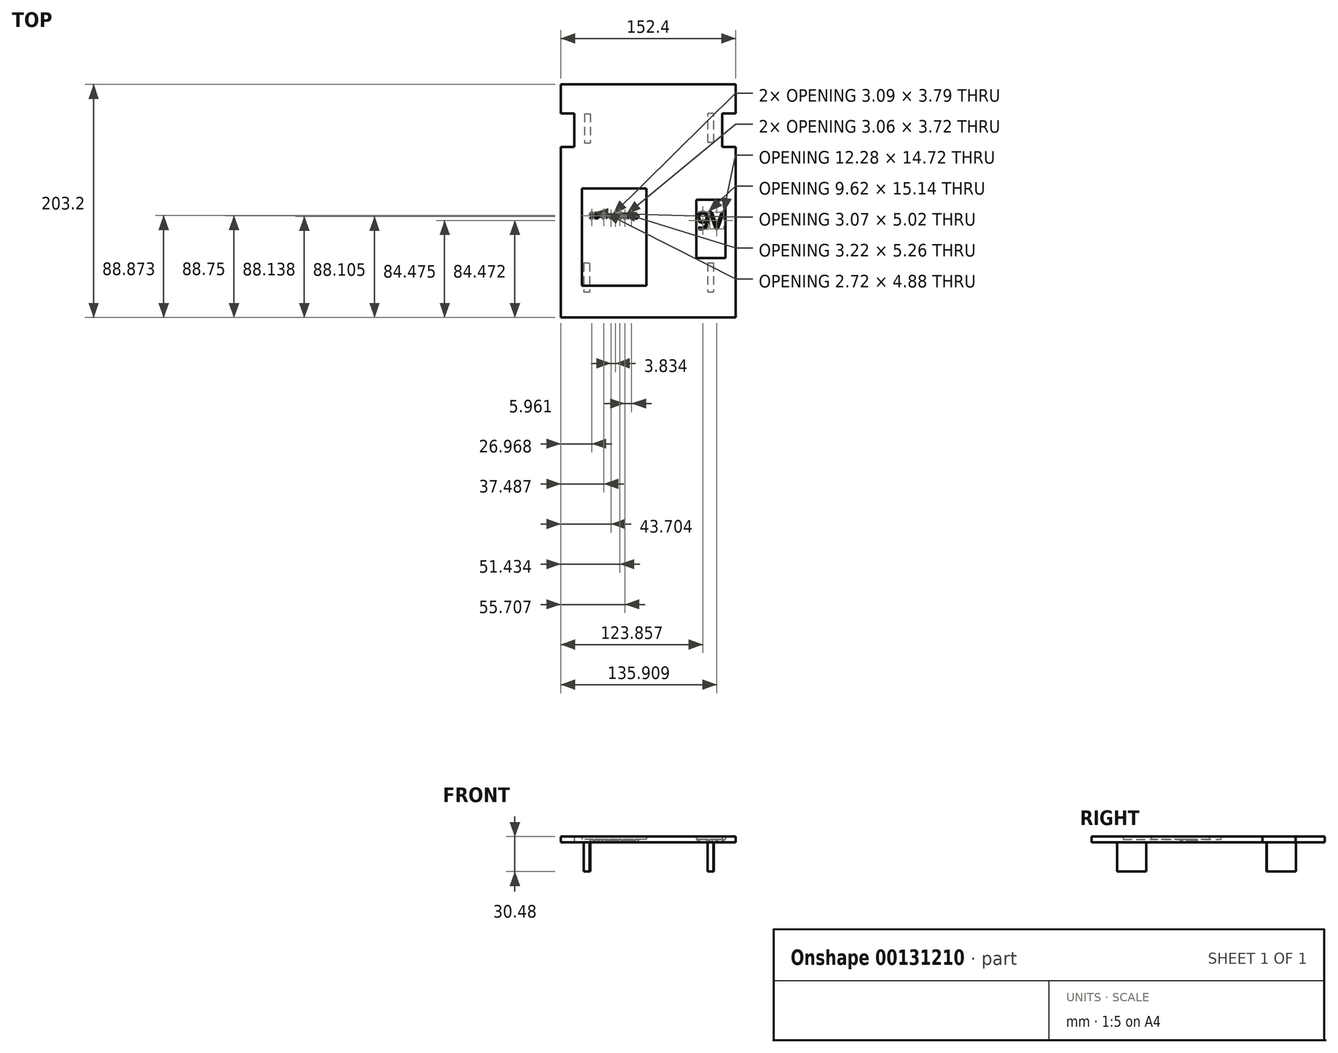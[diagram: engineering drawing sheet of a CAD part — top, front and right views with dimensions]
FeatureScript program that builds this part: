
annotation { "Feature Type Name" : "Feature", "Feature Type Description" : "" }
export const myFeature = defineFeature(function(context is Context, id is Id, definition is map)
    precondition{}
    {
        {
            var Q0;
            Q0=qCreatedBy(makeId("Top.planeOp"),FACE);
            var sketch = newSketch(context, id + "F0", { "sketchPlane" : qUnion([Q0])});
            skLineSegment(sketch, "E0.bottom", {"start": v(60.22, -89.13) * mm, "end": v(-92.18, -89.13) * mm});
            skLineSegment(sketch, "E0.top", {"start": v(60.22, 114.07) * mm, "end": v(-92.18, 114.07) * mm});
            skLineSegment(sketch, "E0.left", {"start": v(60.22, -89.13) * mm, "end": v(60.22, 114.07) * mm});
            skLineSegment(sketch, "E0.right", {"start": v(-92.18, -89.13) * mm, "end": v(-92.18, 114.07) * mm});
            skPoint(sketch, "E0.middle", {"position": v(-15.98, 12.47) * mm});
            skLineSegment(sketch, "E1.bottom", {"start": v(-92.18, 88.67) * mm, "end": v(-80.48, 88.67) * mm});
            skLineSegment(sketch, "E1.top", {"start": v(-92.18, 59.67) * mm, "end": v(-80.48, 59.67) * mm});
            skLineSegment(sketch, "E1.left", {"start": v(-92.18, 88.67) * mm, "end": v(-92.18, 59.67) * mm});
            skLineSegment(sketch, "E1.right", {"start": v(-80.48, 88.67) * mm, "end": v(-80.48, 59.67) * mm});
            skPoint(sketch, "E1.middle", {"position": v(-86.33, 74.17) * mm});
            skLineSegment(sketch, "E2.bottom", {"start": v(60.22, 88.67) * mm, "end": v(48.5, 88.67) * mm});
            skLineSegment(sketch, "E2.top", {"start": v(60.22, 59.66) * mm, "end": v(48.5, 59.66) * mm});
            skLineSegment(sketch, "E2.left", {"start": v(60.22, 88.67) * mm, "end": v(60.22, 59.66) * mm});
            skLineSegment(sketch, "E2.right", {"start": v(48.5, 88.67) * mm, "end": v(48.5, 59.66) * mm});
            skPoint(sketch, "E2.middle", {"position": v(54.36, 74.16) * mm});
            skPoint(sketch, "E3", {"position": v(60.22, 88.67) * mm});
            skLineSegment(sketch, "E4", {"start": v(60.22, 88.67) * mm, "end": v(60.22, 114.07) * mm, "construction": true});
            skLineSegment(sketch, "E5", {"start": v(-92.18, 88.67) * mm, "end": v(-92.18, 114.07) * mm, "construction": true});
            skLineSegment(sketch, "E6.bottom", {"start": v(-17.66, -61.57) * mm, "end": v(-73.66, -61.57) * mm});
            skLineSegment(sketch, "E6.top", {"start": v(-17.66, 23.43) * mm, "end": v(-73.66, 23.43) * mm});
            skLineSegment(sketch, "E6.left", {"start": v(-17.66, -61.57) * mm, "end": v(-17.66, 23.43) * mm});
            skLineSegment(sketch, "E6.right", {"start": v(-73.66, -61.57) * mm, "end": v(-73.66, 23.43) * mm});
            skPoint(sketch, "E6.middle", {"position": v(-45.66, -19.07) * mm});
            skText(sketch, "E7", { "text": "SB-Freeduino", "fontName": "OpenSans-Regular.ttf"});
            skPoint(sketch, "E8", {"position": v(-45.66, 23.43) * mm});
            skLineSegment(sketch, "E9.bottom", {"start": v(25.8, 13.38) * mm, "end": v(51.2, 13.38) * mm});
            skLineSegment(sketch, "E9.top", {"start": v(25.8, -37.42) * mm, "end": v(51.2, -37.42) * mm});
            skLineSegment(sketch, "E9.left", {"start": v(25.8, 13.38) * mm, "end": v(25.8, -37.42) * mm});
            skLineSegment(sketch, "E9.right", {"start": v(51.2, 13.38) * mm, "end": v(51.2, -37.42) * mm});
            skText(sketch, "E10", { "text": "9V", "fontName": "OpenSans-Regular.ttf"});
            skLineSegment(sketch, "E11.bottom", {"start": v(-71.67, 88.52) * mm, "end": v(-66.6, 88.52) * mm});
            skLineSegment(sketch, "E11.top", {"start": v(-71.67, 63.12) * mm, "end": v(-66.6, 63.12) * mm});
            skLineSegment(sketch, "E11.left", {"start": v(-71.67, 88.52) * mm, "end": v(-71.67, 63.12) * mm});
            skLineSegment(sketch, "E11.right", {"start": v(-66.6, 88.52) * mm, "end": v(-66.6, 63.12) * mm});
            skLineSegment(sketch, "E12.bottom", {"start": v(41.07, 63.3) * mm, "end": v(36, 63.3) * mm});
            skLineSegment(sketch, "E12.top", {"start": v(41.07, 88.7) * mm, "end": v(36, 88.7) * mm});
            skLineSegment(sketch, "E12.left", {"start": v(41.07, 63.3) * mm, "end": v(41.07, 88.7) * mm});
            skLineSegment(sketch, "E12.right", {"start": v(36, 63.3) * mm, "end": v(36, 88.7) * mm});
            skPoint(sketch, "E12.middle", {"position": v(38.53, 76) * mm});
            skLineSegment(sketch, "E13.bottom", {"start": v(-67.05, -41.62) * mm, "end": v(-72.13, -41.62) * mm});
            skLineSegment(sketch, "E13.top", {"start": v(-67.05, -67.02) * mm, "end": v(-72.13, -67.02) * mm});
            skLineSegment(sketch, "E13.left", {"start": v(-67.05, -41.62) * mm, "end": v(-67.05, -67.02) * mm});
            skLineSegment(sketch, "E13.right", {"start": v(-72.13, -41.62) * mm, "end": v(-72.13, -67.02) * mm});
            skPoint(sketch, "E13.middle", {"position": v(-69.59, -54.32) * mm});
            skLineSegment(sketch, "E14.bottom", {"start": v(35.62, -41.6) * mm, "end": v(40.7, -41.6) * mm});
            skLineSegment(sketch, "E14.top", {"start": v(35.62, -67) * mm, "end": v(40.7, -67) * mm});
            skLineSegment(sketch, "E14.left", {"start": v(35.62, -41.6) * mm, "end": v(35.62, -67) * mm});
            skLineSegment(sketch, "E14.right", {"start": v(40.7, -41.6) * mm, "end": v(40.7, -67) * mm});
            skPoint(sketch, "E14.middle", {"position": v(38.16, -54.3) * mm});
            const initialGuessF0  = {"E7": [-0.0671, -0.00282, 1, 0, 0.00492], "E10": [0.0258, -0.01202, 1, 0, 0.01485]};
            skSetInitialGuess(sketch, initialGuessF0);
            skSolve(sketch);
        }
        {
            var Q0;
            Q0=makeQuery(id+"F0.imprint","IMPRINT",FACE,{"disambiguationData":[TD([[makeQuery(id+"F0.imprint","IMPRINT",EDGE,{"derivedFrom":sQuery(id+"F0.wireOp",EDGE,"E12.bottom")}),-1.0]])]});
            var Q1;
            {var subQ5=sQuery(id+"F0.wireOp",EDGE,"E0.bottom");Q1=makeQuery(id+"F0.imprint","IMPRINT",FACE,{"disambiguationData":[TD([[makeQuery(id+"F0.imprint","IMPRINT",EDGE,{"derivedFrom":subQ5}),-1.0]])]});}
            var Q2;
            Q2=makeQuery(id+"F0.imprint","IMPRINT",FACE,{"disambiguationData":[TD([[makeQuery(id+"F0.imprint","IMPRINT",EDGE,{"derivedFrom":sQuery(id+"F0.wireOp",EDGE,"E11.bottom")}),-1.0]])]});
            var Q3;
            {var subQ5=sQuery(id+"F0.wireOp",EDGE,"E13.top");Q3=makeQuery(id+"F0.imprint","IMPRINT",FACE,{"disambiguationData":[TD([[makeQuery(id+"F0.imprint","IMPRINT",EDGE,{"derivedFrom":subQ5}),-1.0]])]});}
            var Q4;
            Q4=makeQuery(id+"F0.imprint","IMPRINT",FACE,{"disambiguationData":[TD([[makeQuery(id+"F0.imprint","IMPRINT",EDGE,{"derivedFrom":sQuery(id+"F0.wireOp",EDGE,"E14.bottom")}),-1.0]])]});
            extrude(context, id + "F1", {"entities" : qUnion([Q0, Q1, Q2, Q3, Q4]), "depth" : 5.08 * mm});
        }
        {
            var Q0;
            Q0=makeQuery(id+"F0.imprint","IMPRINT",FACE,{"disambiguationData":[TD([[makeQuery(id+"F0.imprint","IMPRINT",EDGE,{"derivedFrom":sQuery(id+"F0.wireOp",EDGE,"E9.bottom")}),-1.0]])]});
            var Q1;
            {var subQ5=sQuery(id+"F0.wireOp",EDGE,"E13.bottom");Q1=makeQuery(id+"F0.imprint","IMPRINT",FACE,{"disambiguationData":[TD([[makeQuery(id+"F0.imprint","IMPRINT",EDGE,{"derivedFrom":subQ5}),1.0]])]});}
            var Q2;
            Q2=makeQuery(id+"F0.imprint","IMPRINT",FACE,{"disambiguationData":[TD([[makeQuery(id+"F0.imprint","IMPRINT",EDGE,{"derivedFrom":sQuery(id+"F0.wireOp",EDGE,"E10.sketch_text.stroke-16")}),1.0]])]});
            var Q3;
            Q3=makeQuery(id+"F0.imprint","IMPRINT",FACE,{"disambiguationData":[TD([[makeQuery(id+"F0.imprint","IMPRINT",EDGE,{"derivedFrom":sQuery(id+"F0.wireOp",EDGE,"E7.sketch_text.stroke-36")}),1.0]])]});
            var Q4;
            Q4=makeQuery(id+"F0.imprint","IMPRINT",FACE,{"disambiguationData":[TD([[makeQuery(id+"F0.imprint","IMPRINT",EDGE,{"derivedFrom":sQuery(id+"F0.wireOp",EDGE,"E7.sketch_text.stroke-43")}),1.0]])]});
            var Q5;
            Q5=makeQuery(id+"F0.imprint","IMPRINT",FACE,{"disambiguationData":[TD([[makeQuery(id+"F0.imprint","IMPRINT",EDGE,{"derivedFrom":sQuery(id+"F0.wireOp",EDGE,"E7.sketch_text.stroke-91")}),1.0]])]});
            var Q6;
            Q6=makeQuery(id+"F0.imprint","IMPRINT",FACE,{"disambiguationData":[TD([[makeQuery(id+"F0.imprint","IMPRINT",EDGE,{"derivedFrom":sQuery(id+"F0.wireOp",EDGE,"E7.sketch_text.stroke-110")}),1.0]])]});
            var Q7;
            Q7=makeQuery(id+"F0.imprint","IMPRINT",FACE,{"disambiguationData":[TD([[makeQuery(id+"F0.imprint","IMPRINT",EDGE,{"derivedFrom":sQuery(id+"F0.wireOp",EDGE,"E7.sketch_text.stroke-130")}),1.0]])]});
            var Q8;
            Q8=makeQuery(id+"F0.imprint","IMPRINT",FACE,{"disambiguationData":[TD([[makeQuery(id+"F0.imprint","IMPRINT",EDGE,{"derivedFrom":sQuery(id+"F0.wireOp",EDGE,"E7.sketch_text.stroke-194")}),1.0]])]});
            var Q9;
            Q9=makeQuery(id+"F0.imprint","IMPRINT",FACE,{"disambiguationData":[TD([[makeQuery(id+"F0.imprint","IMPRINT",EDGE,{"derivedFrom":sQuery(id+"F0.wireOp",EDGE,"E6.top")}),1.0]])]});
            extrude(context, id + "F2", {"entities" : qUnion([Q0, Q1, Q2, Q3, Q4, Q5, Q6, Q7, Q8, Q9]), "operationType" : NewBodyOperationType.ADD, "depth" : 2.54 * mm});
        }
        {
            var Q0;
            Q0=makeQuery(id+"F0.imprint","IMPRINT",FACE,{"disambiguationData":[TD([[makeQuery(id+"F0.imprint","IMPRINT",EDGE,{"derivedFrom":sQuery(id+"F0.wireOp",EDGE,"E12.bottom")}),-1.0]])]});
            var Q1;
            Q1=makeQuery(id+"F0.imprint","IMPRINT",FACE,{"disambiguationData":[TD([[makeQuery(id+"F0.imprint","IMPRINT",EDGE,{"derivedFrom":sQuery(id+"F0.wireOp",EDGE,"E11.bottom")}),-1.0]])]});
            var Q2;
            Q2=makeQuery(id+"F0.imprint","IMPRINT",FACE,{"disambiguationData":[TD([[makeQuery(id+"F0.imprint","IMPRINT",EDGE,{"derivedFrom":sQuery(id+"F0.wireOp",EDGE,"E14.bottom")}),-1.0]])]});
            var Q3;
            {var subQ5=sQuery(id+"F0.wireOp",EDGE,"E13.bottom");Q3=makeQuery(id+"F0.imprint","IMPRINT",FACE,{"disambiguationData":[TD([[makeQuery(id+"F0.imprint","IMPRINT",EDGE,{"derivedFrom":subQ5}),1.0]])]});}
            var Q4;
            {var subQ5=sQuery(id+"F0.wireOp",EDGE,"E13.top");Q4=makeQuery(id+"F0.imprint","IMPRINT",FACE,{"disambiguationData":[TD([[makeQuery(id+"F0.imprint","IMPRINT",EDGE,{"derivedFrom":subQ5}),-1.0]])]});}
            extrude(context, id + "F3", {"entities" : qUnion([Q0, Q1, Q2, Q3, Q4]), "operationType" : NewBodyOperationType.ADD, "oppositeDirection" : true, "depth" : 25.4 * mm});
        }
    });
